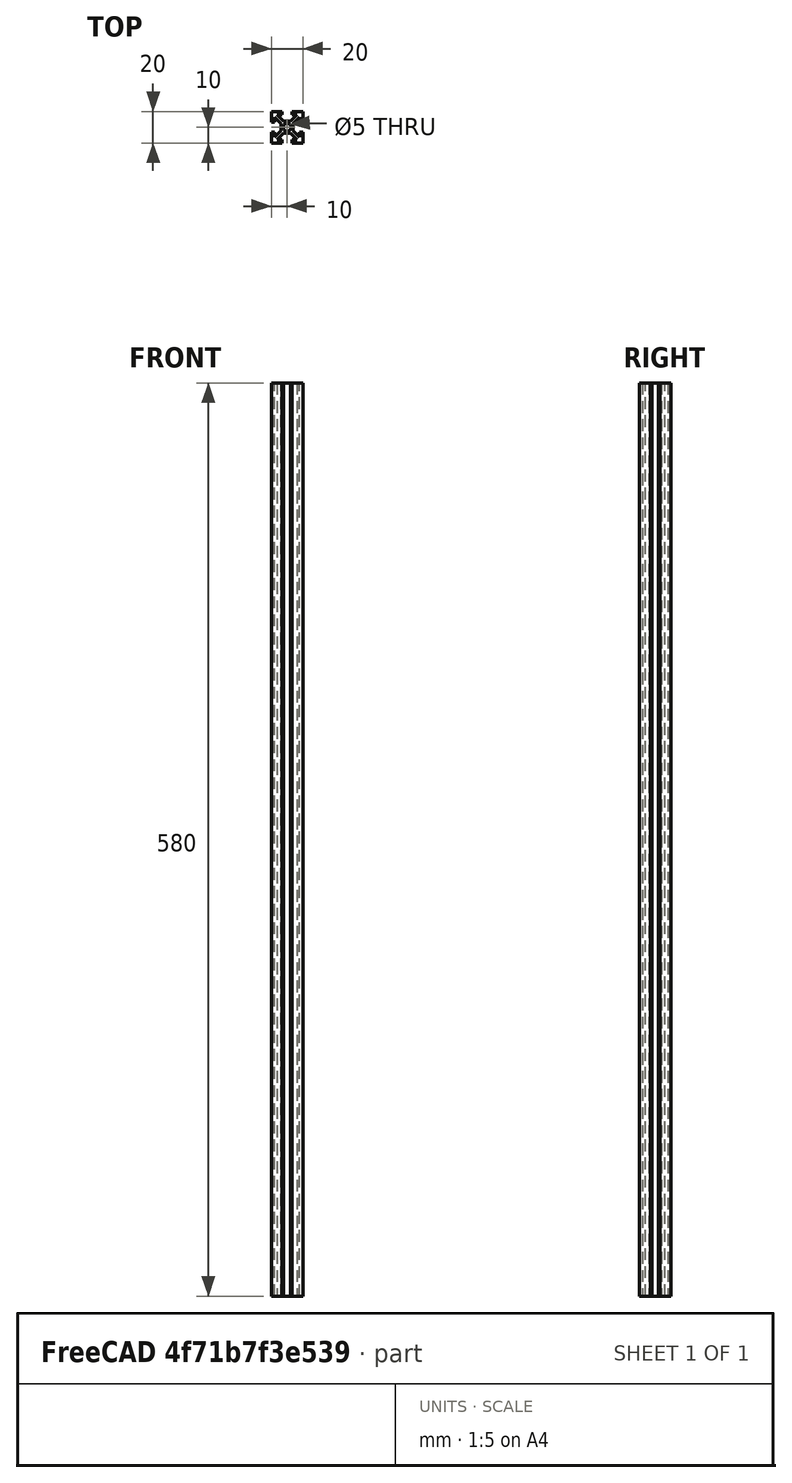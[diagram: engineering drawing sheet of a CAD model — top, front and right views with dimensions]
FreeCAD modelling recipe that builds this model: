
FCSTD DOCUMENT  (FreeCAD 1.0R39109 (Git))
Label: T-Slot_20_height
License: All rights reserved
LicenseURL: http://en.wikipedia.org/wiki/All_rights_reserved
objects: Sketcher::SketchObject×3, TechDraw::DrawViewDimension×3, PartDesign::Pocket×2, TechDraw::DrawProjGroupItem×2, PartDesign::Pad×1, PartDesign::Body×1, TechDraw::DrawSVGTemplate×1, TechDraw::DrawProjGroup×1, TechDraw::DrawPage×1
note: 22 computed .brp shape members not serialized (recipe doc carries the construction recipe); baked Part::Feature solids carry a one-line shape summary decoded from their .brp

FEATURE [Sketcher::SketchObject] Sketch
  ArcFitTolerance = 0
  AttachmentSupport = -> [XY_Plane]
  FullyConstrained = true
  MakeInternals = false
  MapMode = 5
  sketch-geometry (4):
    g0: LineSegment StartX=-10 StartY=10 StartZ=0 EndX=10 EndY=10 EndZ=0
    g1: LineSegment StartX=10 StartY=10 StartZ=0 EndX=10 EndY=-10 EndZ=0
    g2: LineSegment StartX=10 StartY=-10 StartZ=0 EndX=-10 EndY=-10 EndZ=0
    g3: LineSegment StartX=-10 StartY=-10 StartZ=0 EndX=-10 EndY=10 EndZ=0
  constraints (10):
    c: Coincident(g0,g1)
    c: Coincident(g1,g2)
    c: Coincident(g2,g3)
    c: Coincident(g3,g0)
    c: Horizontal(g0)
    c: Vertical(g1)
    c: Symmetric(g2,g1,g-2)
    c: Symmetric(g0,g2,g-1)
    c: Equal(g3,g2)
    c: Distance(g0) = 20
FEATURE [PartDesign::Pad] Pad  label="Change Length Here!"
  AllowMultiFace = false
  Direction = (0,0,1)
  Length = 580
  Length2 = 100
  Profile = -> Sketch
  ReferenceAxis = -> Sketch [N_Axis]
  Refine = true
  Suppressed = false
  Type = 0
FEATURE [Sketcher::SketchObject] Sketch001
  ArcFitTolerance = 0
  AttachmentSupport = -> [Pad]
  ExternalGeometry = -> [Pad]
  FullyConstrained = false
  MakeInternals = false
  MapMode = 5
  Placement = pos=(0,0,580) rot=(0,0,1;0rad)
  sketch-geometry (23):
    g0: LineSegment StartX=-3.1 StartY=10 StartZ=0 EndX=3.1 EndY=10 EndZ=0
    g1: LineSegment StartX=3.1 StartY=10 StartZ=0 EndX=3.1 EndY=8 EndZ=0
    g2: LineSegment [constr] StartX=3.1 StartY=8 StartZ=0 EndX=-3.1 EndY=8 EndZ=0
    g3: LineSegment StartX=-3.1 StartY=8 StartZ=0 EndX=-3.1 EndY=10 EndZ=0
    g4: LineSegment StartX=-3.1 StartY=8 StartZ=0 EndX=-6.23223 EndY=8 EndZ=0
    g5: LineSegment StartX=-6.23223 StartY=8 StartZ=0 EndX=-2.13223 EndY=3.9 EndZ=0
    g6: LineSegment StartX=-2.13223 StartY=3.9 StartZ=0 EndX=2.13223 EndY=3.9 EndZ=0
    g7: LineSegment StartX=2.13223 StartY=3.9 StartZ=0 EndX=6.23223 EndY=8 EndZ=0
    g8: LineSegment StartX=6.23223 StartY=8 StartZ=0 EndX=3.1 EndY=8 EndZ=0
    g9: LineSegment [constr] StartX=-3.9 StartY=3.9 StartZ=0 EndX=3.9 EndY=3.9 EndZ=0
    g10: LineSegment [constr] StartX=3.9 StartY=3.9 StartZ=0 EndX=3.9 EndY=-3.9 EndZ=0
    g11: LineSegment [constr] StartX=3.9 StartY=-3.9 StartZ=0 EndX=-3.9 EndY=-3.9 EndZ=0
    g12: LineSegment [constr] StartX=-3.9 StartY=-3.9 StartZ=0 EndX=-3.9 EndY=3.9 EndZ=0
    g13: Circle CenterX=0 CenterY=0 CenterZ=0 NormalX=0 NormalY=0 NormalZ=1 AngleXU=0 Radius=2.5
    g14: LineSegment [constr] StartX=3.9 StartY=3.9 StartZ=0 EndX=3.01612 EndY=4.78388 EndZ=0
    g15: LineSegment StartX=-3.1 StartY=-8 StartZ=0 EndX=-6.23223 EndY=-8 EndZ=0
    g16: LineSegment StartX=6.23223 StartY=-8 StartZ=0 EndX=3.1 EndY=-8 EndZ=0
    g17: LineSegment StartX=3.1 StartY=-10 StartZ=0 EndX=3.1 EndY=-8 EndZ=0
    g18: LineSegment StartX=-3.1 StartY=-10 StartZ=0 EndX=3.1 EndY=-10 EndZ=0
    g19: LineSegment StartX=-3.1 StartY=-8 StartZ=0 EndX=-3.1 EndY=-10 EndZ=0
    g20: LineSegment StartX=-6.23223 StartY=-8 StartZ=0 EndX=-2.13223 EndY=-3.9 EndZ=0
    g21: LineSegment StartX=-2.13223 StartY=-3.9 StartZ=0 EndX=2.13223 EndY=-3.9 EndZ=0
    g22: LineSegment StartX=2.13223 StartY=-3.9 StartZ=0 EndX=6.23223 EndY=-8 EndZ=0
  constraints (55):
    c: Coincident(g0,g1)
    c: Coincident(g1,g2)
    c: Coincident(g2,g3)
    c: Coincident(g3,g0)
    c: Horizontal(g2)
    c: Vertical(g1)
    c: Vertical(g3)
    c: PointOnObject(g0,g-3)
    c: Symmetric(g0,g0,g-2)
    c: Distance(g0) = 6.2
    c: Distance(g3) = 2
    c: Coincident(g3,g4)
    c: Horizontal(g4)
    c: Coincident(g4,g5)
    c: Coincident(g5,g6)
    c: Coincident(g6,g7)
    c: Coincident(g7,g8)
    c: Coincident(g8,g1)
    c: Horizontal(g8)
    c: Symmetric(g5,g6,g-2)
    c: Equal(g4,g8)
    c: Coincident(g9,g10)
    c: Coincident(g10,g11)
    c: Coincident(g11,g12)
    c: Coincident(g12,g9)
    c: Horizontal(g9)
    c: Vertical(g12)
    c: Equal(g9,g12)
    c: Symmetric(g11,g10,g-2)
    c: Symmetric(g9,g10,g-1)
    c: Distance(g9) = 7.8
    c: Coincident(g13,g-1)
    c: Radius(g13) = 2.5
    c: DistanceY(g6,g0) = 6.1
    c: Coincident(g14,g9)
    c: PointOnObject(g14,g7)
    c: Perpendicular(g7,g14)
    c: Distance(g14) = 1.25
    c: Angle(g6,g5) = 2.35619
    c: Coincident(g18,g17)
    c: Coincident(g19,g18)
    c: Vertical(g17)
    c: Vertical(g19)
    c: Distance(g18) = 6.2
    c: Distance(g19) = 2
    c: Coincident(g19,g15)
    c: Horizontal(g15)
    c: Coincident(g15,g20)
    c: Coincident(g20,g21)
    c: Coincident(g21,g22)
    c: Coincident(g22,g16)
    c: Coincident(g16,g17)
    c: Horizontal(g16)
    c: Equal(g15,g16)
    c: Angle(g21,g20) = -2.35619
FEATURE [PartDesign::Pocket] Pocket  label="Top & Bottom Slots"
  AllowMultiFace = false
  BaseFeature = -> Pad
  Direction = (0,0,-1)
  Length = 5
  Length2 = 100
  Profile = -> Sketch001
  Refine = true
  Suppressed = false
  Type = 1
FEATURE [Sketcher::SketchObject] Sketch002
  ArcFitTolerance = 0
  AttachmentSupport = -> [Pocket]
  ExternalGeometry = -> [Pocket]
  FullyConstrained = false
  MakeInternals = false
  MapMode = 5
  Placement = pos=(0,0,0) rot=(1,0,0;3.14159rad)
  sketch-geometry (19):
    g0: LineSegment StartX=-10 StartY=-3.1 StartZ=0 EndX=-8 EndY=-3.1 EndZ=0
    g1: LineSegment [constr] StartX=-8 StartY=-3.1 StartZ=0 EndX=-8 EndY=3.1 EndZ=0
    g2: LineSegment StartX=-8 StartY=3.1 StartZ=0 EndX=-10 EndY=3.1 EndZ=0
    g3: LineSegment StartX=-10 StartY=3.1 StartZ=0 EndX=-10 EndY=-3.1 EndZ=0
    g4: LineSegment StartX=-8 StartY=-3.1 StartZ=0 EndX=-8 EndY=-6.23223 EndZ=0
    g5: LineSegment StartX=-8 StartY=-6.23223 StartZ=0 EndX=-3.9 EndY=-2.13223 EndZ=0
    g6: LineSegment StartX=-3.9 StartY=-2.13223 StartZ=0 EndX=-3.9 EndY=2.13223 EndZ=0
    g7: LineSegment StartX=-3.9 StartY=2.13223 StartZ=0 EndX=-8 EndY=6.23223 EndZ=0
    g8: LineSegment StartX=-8 StartY=6.23223 StartZ=0 EndX=-8 EndY=3.1 EndZ=0
    g9: LineSegment [constr] StartX=-2.13223 StartY=3.9 StartZ=0 EndX=-3.9 EndY=2.13223 EndZ=0
    g10: LineSegment [constr] StartX=2.13223 StartY=3.9 StartZ=0 EndX=3.9 EndY=2.13223 EndZ=0
    g11: LineSegment StartX=3.9 StartY=-2.13223 StartZ=0 EndX=3.9 EndY=2.13223 EndZ=0
    g12: LineSegment StartX=8 StartY=-6.23223 StartZ=0 EndX=3.9 EndY=-2.13223 EndZ=0
    g13: LineSegment StartX=3.9 StartY=2.13223 StartZ=0 EndX=8 EndY=6.23223 EndZ=0
    g14: LineSegment StartX=8 StartY=6.23223 StartZ=0 EndX=8 EndY=3.1 EndZ=0
    g15: LineSegment StartX=8 StartY=3.1 StartZ=0 EndX=10 EndY=3.1 EndZ=0
    g16: LineSegment StartX=10 StartY=3.1 StartZ=0 EndX=10 EndY=-3.1 EndZ=0
    g17: LineSegment StartX=10 StartY=-3.1 StartZ=0 EndX=8 EndY=-3.1 EndZ=0
    g18: LineSegment StartX=8 StartY=-3.1 StartZ=0 EndX=8 EndY=-6.23223 EndZ=0
  constraints (43):
    c: Coincident(g0,g1)
    c: Coincident(g1,g2)
    c: Coincident(g2,g3)
    c: Coincident(g3,g0)
    c: Horizontal(g0)
    c: Horizontal(g2)
    c: Vertical(g1)
    c: PointOnObject(g0,g-3)
    c: Symmetric(g2,g0,g-1)
    c: Distance(g3) = 6.2
    c: Distance(g0) = 2
    c: Coincident(g0,g4)
    c: Vertical(g4)
    c: Coincident(g4,g5)
    c: Coincident(g5,g6)
    c: Coincident(g6,g7)
    c: Coincident(g7,g8)
    c: Coincident(g8,g2)
    c: Vertical(g8)
    c: Equal(g4,g8)
    c: Symmetric(g6,g5,g-1)
    c: DistanceX(g2,g6) = 6.1
    c: Angle(g6,g5) = 2.35619
    c: Coincident(g9,g-4)
    c: Perpendicular(g-4,g9)
    c: Coincident(g6,g9)
    c: Coincident(g15,g16)
    c: Coincident(g16,g17)
    c: Horizontal(g17)
    c: Horizontal(g15)
    c: Distance(g16) = 6.2
    c: Distance(g17) = 2
    c: Coincident(g17,g18)
    c: Vertical(g18)
    c: Coincident(g18,g12)
    c: Coincident(g12,g11)
    c: Coincident(g11,g13)
    c: Coincident(g13,g14)
    c: Coincident(g14,g15)
    c: Vertical(g14)
    c: Equal(g18,g14)
    c: Angle(g11,g12) = -2.35619
    c: Coincident(g11,g10)
FEATURE [PartDesign::Pocket] Pocket001  label="R&L Slots"
  AllowMultiFace = false
  BaseFeature = -> Pocket
  Direction = (0,0,1)
  Length = 5
  Length2 = 100
  Profile = -> Sketch002
  Refine = true
  Suppressed = false
  Type = 1
FEATURE [PartDesign::Body] Body  label="Tslot20_heigh"
  AllowCompound = false
  Group = -> [Sketch,Pad,Sketch001,Pocket,Sketch002,Pocket001]
  Origin = -> Origin
  Tip = -> Pocket001
FEATURE [TechDraw::DrawSVGTemplate] Template
  EditableTexts = approval_person=B. Hecate; creator=Djordje Vujic; date_of_issue=1/21/2025; document_type=Assembly Drawing; general_tolerances=ISO 2768-m; identification_number=DN; language_code=EN; part_material=Stainless steel Mat.No. 1.4301; revision_index=AAA; sheet_number=1 / 4; sheet_scale=1 : 3; title=T-Slot_20_height
  Height = 297
  Orientation = 0
  Template = D:/Program Files/FreeCAD 1.0/data/Mod/TechDraw/Templates/A4_Portrait_ISO5457_minimal.svg
  Width = 210
FEATURE [TechDraw::DrawProjGroupItem] ProjItem  label="Front"
  CoarseView = false
  Direction = (0,-1,0)
  Focus = 100
  HardHidden = false
  IsoCount = 0
  IsoHidden = false
  IsoVisible = false
  LockPosition = true
  Perspective = false
  Rotation = 0
  RotationVector = (1,0,0)
  Scale = 0.333333
  ScaleType = 2
  ScrubCount = 1
  SeamHidden = false
  SeamVisible = false
  SmoothHidden = false
  SmoothVisible = true
  Source = -> [Body]
  Type = 0
  X = 0
  XDirection = (1,0,0)
  Y = 0
FEATURE [TechDraw::DrawProjGroupItem] ProjItem001  label="Bottom"
  CoarseView = false
  Direction = (0,0,-1)
  Focus = 100
  HardHidden = false
  IsoCount = 0
  IsoHidden = false
  IsoVisible = false
  LockPosition = false
  Perspective = false
  Rotation = 0
  RotationVector = (1,0,0)
  Scale = 0.333333
  ScaleType = 2
  ScrubCount = 1
  SeamHidden = false
  SeamVisible = false
  SmoothHidden = false
  SmoothVisible = true
  Source = -> [Body]
  Type = 5
  X = 0
  XDirection = (1,0,0)
  Y = 115
FEATURE [TechDraw::DrawProjGroup] ProjGroup
  Anchor = -> ProjItem
  AutoDistribute = true
  LockPosition = false
  ProjectionType = 0
  Rotation = 0
  Scale = 0.333333
  ScaleType = 2
  Source = -> [Body]
  Views = -> [ProjItem,ProjItem001]
  X = 107.297
  Y = 159.41
  spacingX = 15
  spacingY = 15
FEATURE [TechDraw::DrawViewDimension] Dimension
  AngleOverride = false
  Arbitrary = false
  ArbitraryTolerances = false
  BoxCorners = (2) [(-3.33333,-3.33333,0),(3.33333,3.33333,0)]
  EqualTolerance = true
  ExtensionAngle = 0
  FormatSpec = %.2w
  FormatSpecOverTolerance = %+.2w
  FormatSpecUnderTolerance = %+.2w
  Inverted = false
  LineAngle = 0
  LockPosition = false
  MeasureType = 1
  OverTolerance = 0
  References2D = -> [ProjItem001]
  Rotation = 0
  ScaleType = 0
  TheoreticalExact = false
  Type = 0
  UnderTolerance = 0
  X = -10.1772
  Y = -5.35989
FEATURE [TechDraw::DrawViewDimension] Dimension001
  AngleOverride = false
  Arbitrary = false
  ArbitraryTolerances = false
  BoxCorners = (2) [(-3.33333,-96.6666,0),(3.33333,96.6666,0)]
  EqualTolerance = true
  ExtensionAngle = 0
  FormatSpec = %.2w
  FormatSpecOverTolerance = %+.2w
  FormatSpecUnderTolerance = %+.2w
  Inverted = false
  LineAngle = 0
  LockPosition = false
  MeasureType = 1
  OverTolerance = 0
  References2D = -> [ProjItem]
  Rotation = 0
  ScaleType = 0
  TheoreticalExact = false
  Type = 2
  UnderTolerance = 0
  X = -56.3813
  Y = 3.94419
FEATURE [TechDraw::DrawViewDimension] Dimension002
  AngleOverride = false
  Arbitrary = false
  ArbitraryTolerances = false
  BoxCorners = (2) [(-3.33333,-3.33333,0),(3.33333,3.33333,0)]
  EqualTolerance = true
  ExtensionAngle = 0
  FormatSpec = %.2w
  FormatSpecOverTolerance = %+.2w
  FormatSpecUnderTolerance = %+.2w
  Inverted = false
  LineAngle = 0
  LockPosition = false
  MeasureType = 1
  OverTolerance = 0
  References2D = -> [ProjItem001]
  Rotation = 0
  ScaleType = 0
  TheoreticalExact = false
  Type = 2
  UnderTolerance = 0
  X = 23.6969
  Y = -8.1912
FEATURE [TechDraw::DrawPage] Page
  KeepUpdated = true
  NextBalloonIndex = 1
  ProjectionType = 0
  Template = -> Template
  Views = -> [ProjGroup,Dimension,Dimension001,Dimension002]
